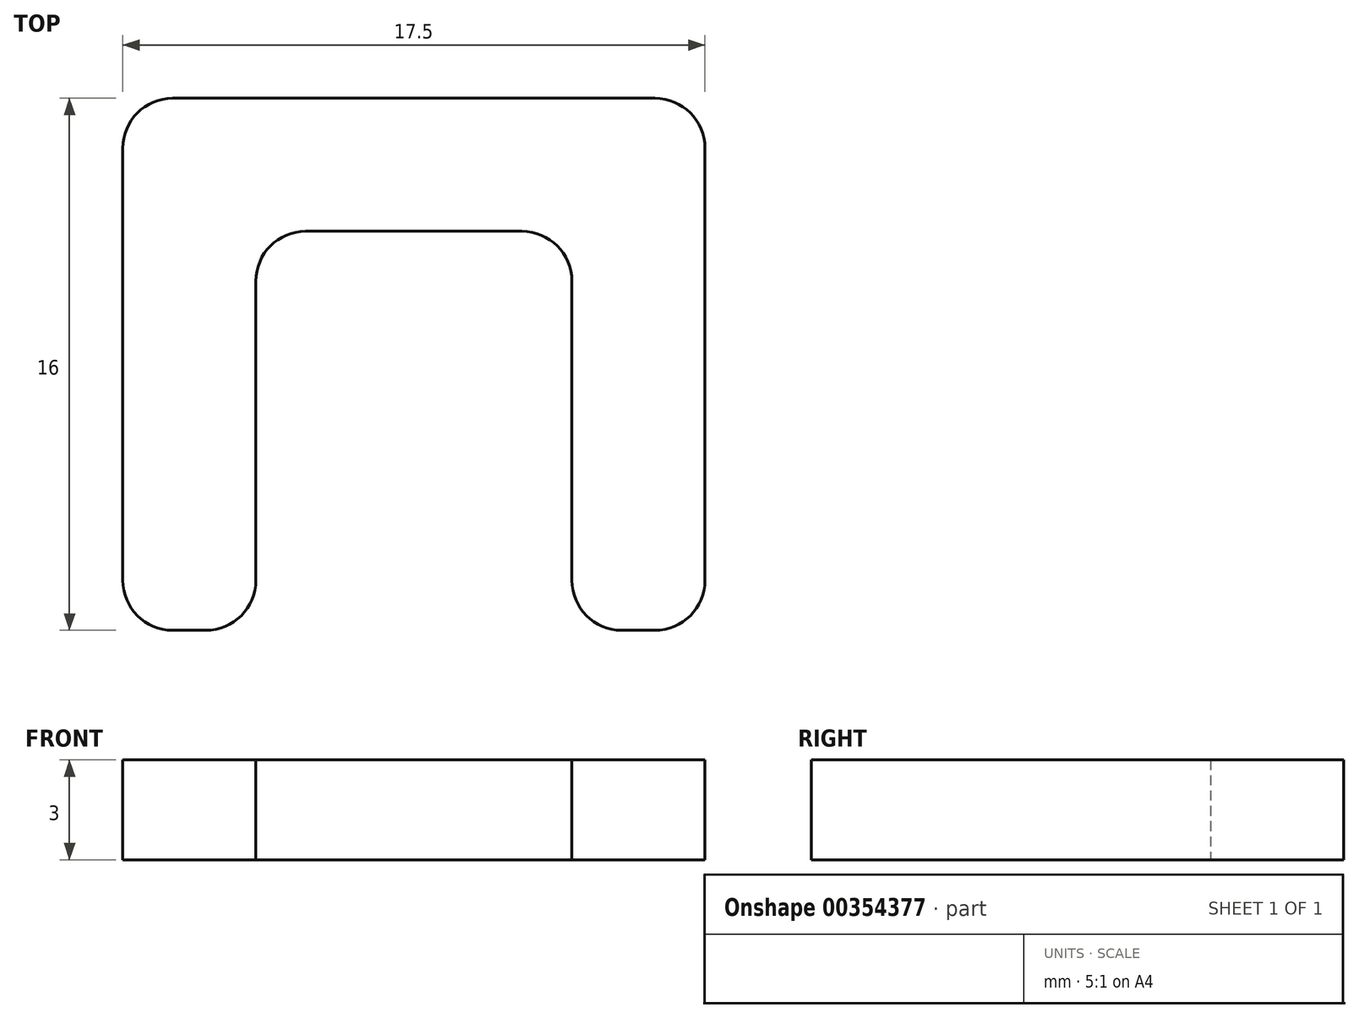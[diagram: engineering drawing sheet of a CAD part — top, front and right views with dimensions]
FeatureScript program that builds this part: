
annotation { "Feature Type Name" : "Feature", "Feature Type Description" : "" }
export const myFeature = defineFeature(function(context is Context, id is Id, definition is map)
    precondition{}
    {
        {
            var Q0;
            Q0=qCreatedBy(makeId("Top.planeOp"),FACE);
            var sketch = newSketch(context, id + "F0", { "sketchPlane" : qUnion([Q0])});
            skLineSegment(sketch, "E0.top", {"start": v(0, 12) * mm, "end": v(9.5, 12) * mm});
            skLineSegment(sketch, "E0.left", {"start": v(0, 0) * mm, "end": v(0, 12) * mm});
            skLineSegment(sketch, "E0.right", {"start": v(9.5, 0) * mm, "end": v(9.5, 12) * mm});
            skLineSegment(sketch, "E1.0", {"start": v(13.5, 0) * mm, "end": v(13.5, 16) * mm});
            skLineSegment(sketch, "E1.1", {"start": v(-4, 16) * mm, "end": v(13.5, 16) * mm});
            skLineSegment(sketch, "E1.2", {"start": v(-4, 0) * mm, "end": v(-4, 16) * mm});
            skLineSegment(sketch, "E2", {"start": v(-4, 0) * mm, "end": v(0, 0) * mm});
            skLineSegment(sketch, "E3", {"start": v(13.5, 0) * mm, "end": v(9.5, 0) * mm});
            skSolve(sketch);
        }
        {
            var Q0;
            Q0 = qSketchRegion(id + "F0", true);
            extrude(context, id + "F1", {"entities" : qUnion([Q0]), "depth" : 3 * mm});
        }
        {
            var Q0;
            Q0=makeQuery(id+"F1.opExtrude","SWEPT_EDGE",EDGE,{"disambiguationData":[OSD([sQuery(id+"F0.wireOp",EDGE,"E0.top"),sQuery(id+"F0.wireOp",EDGE,"E0.right")])]});
            var Q1;
            Q1=makeQuery(id+"F1.opExtrude","SWEPT_EDGE",EDGE,{"disambiguationData":[OSD([sQuery(id+"F0.wireOp",EDGE,"E0.top"),sQuery(id+"F0.wireOp",EDGE,"E0.left")])]});
            var Q2;
            Q2=makeQuery(id+"F1.opExtrude","SWEPT_EDGE",EDGE,{"disambiguationData":[OSD([sQuery(id+"F0.wireOp",EDGE,"E1.1"),sQuery(id+"F0.wireOp",EDGE,"E1.2")])]});
            var Q3;
            Q3=makeQuery(id+"F1.opExtrude","SWEPT_EDGE",EDGE,{"disambiguationData":[OSD([sQuery(id+"F0.wireOp",EDGE,"E1.0"),sQuery(id+"F0.wireOp",EDGE,"E1.1")])]});
            var Q4;
            Q4=makeQuery(id+"F1.opExtrude","SWEPT_EDGE",EDGE,{"disambiguationData":[OSD([sQuery(id+"F0.wireOp",EDGE,"E0.left"),sQuery(id+"F0.wireOp",EDGE,"E2")])]});
            var Q5;
            Q5=makeQuery(id+"F1.opExtrude","SWEPT_EDGE",EDGE,{"disambiguationData":[OSD([sQuery(id+"F0.wireOp",EDGE,"E0.right"),sQuery(id+"F0.wireOp",EDGE,"E3")])]});
            var Q6;
            Q6=makeQuery(id+"F1.opExtrude","SWEPT_EDGE",EDGE,{"disambiguationData":[OSD([sQuery(id+"F0.wireOp",EDGE,"E1.2"),sQuery(id+"F0.wireOp",EDGE,"E2")])]});
            var Q7;
            Q7=makeQuery(id+"F1.opExtrude","SWEPT_EDGE",EDGE,{"disambiguationData":[OSD([sQuery(id+"F0.wireOp",EDGE,"E1.0"),sQuery(id+"F0.wireOp",EDGE,"E3")])]});
            fillet(context, id + "F2", {"entities" : qUnion([Q0, Q1, Q2, Q3, Q4, Q5, Q6, Q7]), "radius" : 1.5 * mm, "tangentPropagation" : true, "allowEdgeOverflow" : false});
        }
    });
